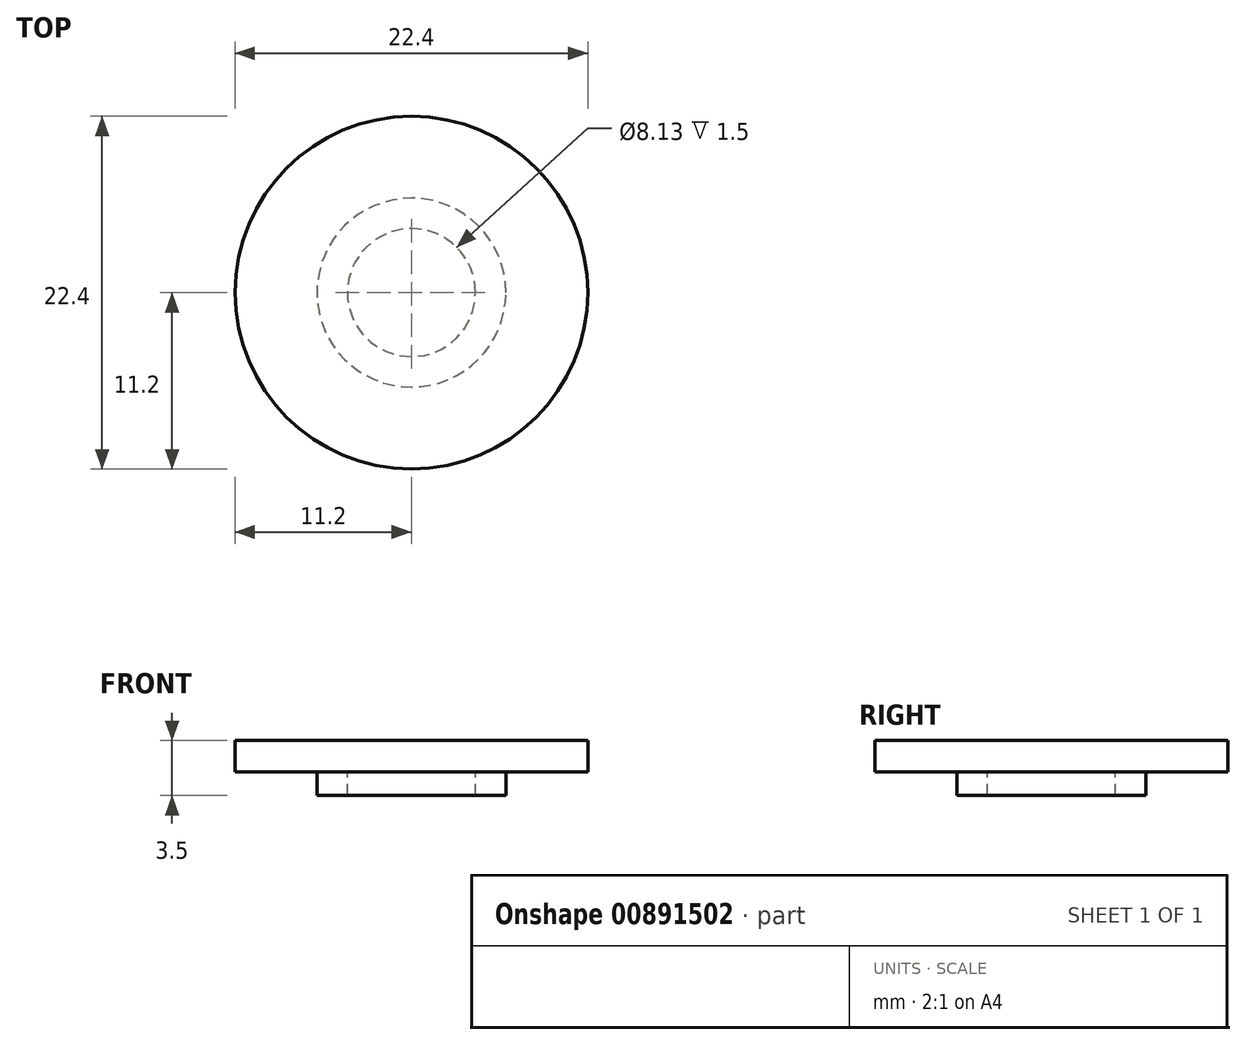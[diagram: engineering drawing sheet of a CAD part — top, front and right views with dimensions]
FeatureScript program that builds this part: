
annotation { "Feature Type Name" : "Feature", "Feature Type Description" : "" }
export const myFeature = defineFeature(function(context is Context, id is Id, definition is map)
    precondition{}
    {
        {
            var Q0;
            Q0=qCreatedBy(makeId("Top.planeOp"),FACE);
            var sketch = newSketch(context, id + "F0", { "sketchPlane" : qUnion([Q0])});
            skCircle(sketch, "E0", {"center": v(0, 0) * mm, "radius": 11.2 * mm});
            skSolve(sketch);
        }
        {
            var Q0;
            Q0 = qSketchRegion(id + "F0", true);
            extrude(context, id + "F1", {"entities" : qUnion([Q0]), "depth" : 2 * mm, "offsetDistance" : 25 * mm});
        }
        {
            var Q0;
            Q0=makeQuery(id+"F1.opExtrude","CAP_FACE",FACE,{"disambiguationData":[OSD([sQuery(id+"F0.wireOp",EDGE,"E0")])],"isStart":true});
            var sketch = newSketch(context, id + "F2", { "sketchPlane" : qUnion([Q0])});
            skCircle(sketch, "E1", {"center": v(0, 0) * mm, "radius": 6 * mm});
            skCircle(sketch, "E2", {"center": v(0, 0) * mm, "radius": 4.06 * mm});
            skSolve(sketch);
        }
        {
            var Q0;
            Q0=makeQuery(id+"F2.imprint","IMPRINT",FACE,{"disambiguationData":[TD([[makeQuery(id+"F2.imprint","IMPRINT",EDGE,{"derivedFrom":sQuery(id+"F2.wireOp",EDGE,"E1")}),1.0]])]});
            extrude(context, id + "F3", {"entities" : qUnion([Q0]), "operationType" : NewBodyOperationType.ADD, "depth" : 1.5 * mm, "offsetDistance" : 25 * mm});
        }
    });
